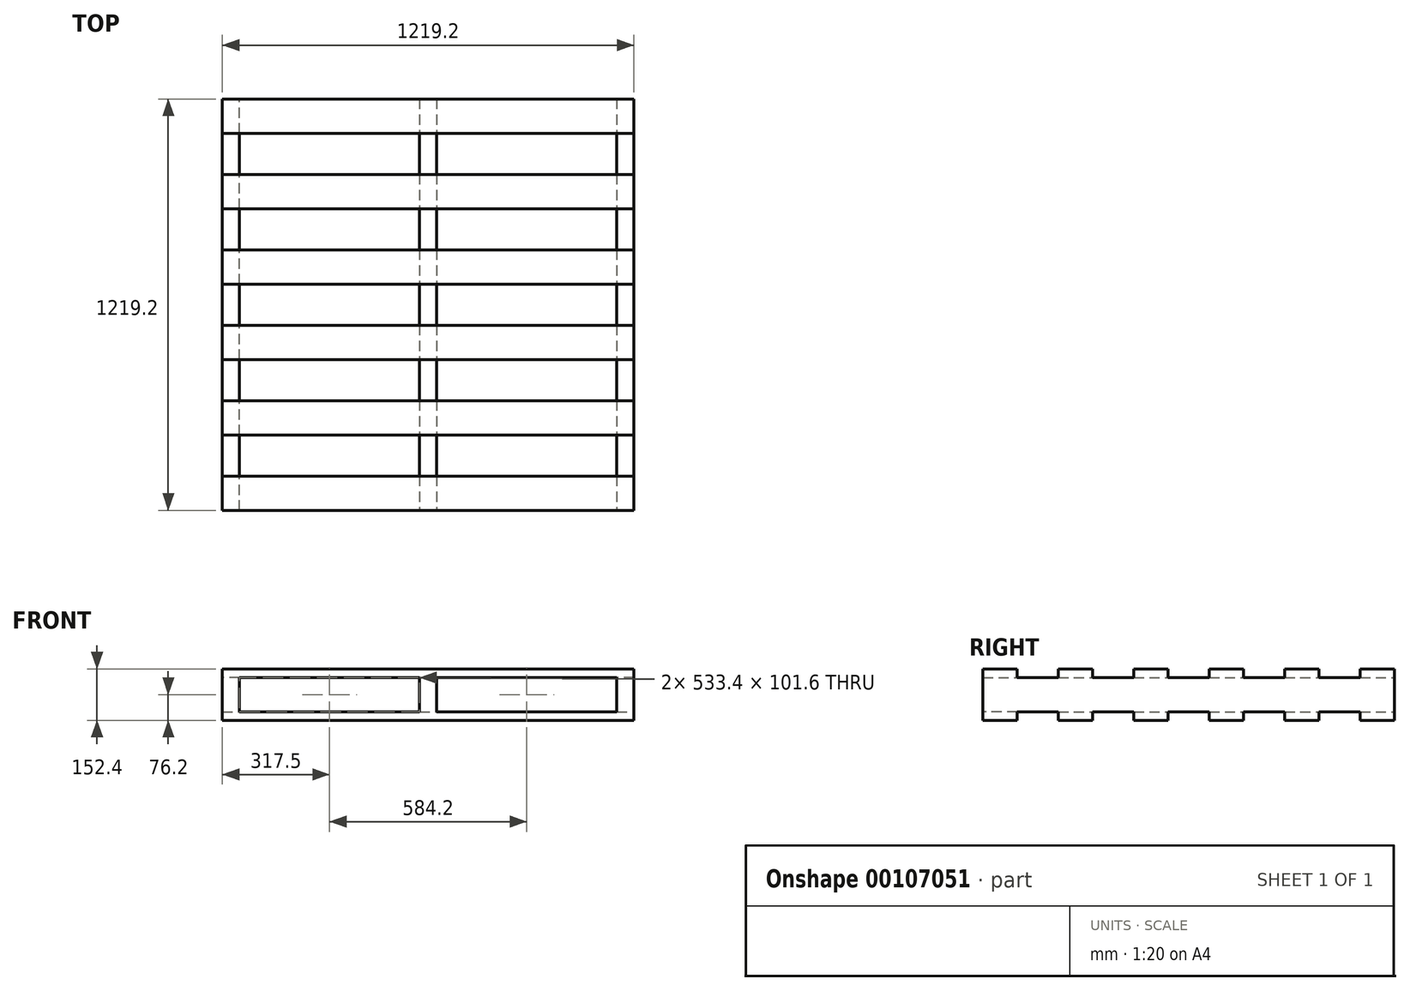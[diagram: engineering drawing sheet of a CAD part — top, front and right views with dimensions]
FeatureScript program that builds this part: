
annotation { "Feature Type Name" : "Feature", "Feature Type Description" : "" }
export const myFeature = defineFeature(function(context is Context, id is Id, definition is map)
    precondition{}
    {
        {
            var Q0;
            Q0=qCreatedBy(makeId("Top.planeOp"),FACE);
            var sketch = newSketch(context, id + "F0", { "sketchPlane" : qUnion([Q0])});
            skLineSegment(sketch, "E0.bottom", {"start": v(0, 0) * mm, "end": v(1219.2, 0) * mm, "construction": true});
            skLineSegment(sketch, "E0.top", {"start": v(0, 1219.2) * mm, "end": v(1219.2, 1219.2) * mm, "construction": true});
            skLineSegment(sketch, "E0.left", {"start": v(0, 0) * mm, "end": v(0, 1219.2) * mm, "construction": true});
            skLineSegment(sketch, "E0.right", {"start": v(1219.2, 0) * mm, "end": v(1219.2, 1219.2) * mm, "construction": true});
            skLineSegment(sketch, "E1.bottom", {"start": v(0, 0) * mm, "end": v(1219.2, 0) * mm});
            skLineSegment(sketch, "E1.top", {"start": v(0, 101.6) * mm, "end": v(1219.2, 101.6) * mm});
            skLineSegment(sketch, "E1.left", {"start": v(0, 0) * mm, "end": v(0, 101.6) * mm});
            skLineSegment(sketch, "E1.right", {"start": v(1219.2, 0) * mm, "end": v(1219.2, 101.6) * mm});
            skLineSegment(sketch, "E2.bottom", {"start": v(0, 325.12) * mm, "end": v(1219.2, 325.12) * mm});
            skLineSegment(sketch, "E2.top", {"start": v(0, 223.52) * mm, "end": v(1219.2, 223.52) * mm});
            skLineSegment(sketch, "E2.left", {"start": v(0, 325.12) * mm, "end": v(0, 223.52) * mm});
            skLineSegment(sketch, "E2.right", {"start": v(1219.2, 325.12) * mm, "end": v(1219.2, 223.52) * mm});
            skLineSegment(sketch, "E3", {"start": v(609.6, 101.6) * mm, "end": v(609.6, 223.52) * mm});
            skLineSegment(sketch, "E4.bottom", {"start": v(0, 447.04) * mm, "end": v(1219.2, 447.04) * mm});
            skLineSegment(sketch, "E4.top", {"start": v(0, 548.64) * mm, "end": v(1219.2, 548.64) * mm});
            skLineSegment(sketch, "E4.left", {"start": v(0, 447.04) * mm, "end": v(0, 548.64) * mm});
            skLineSegment(sketch, "E4.right", {"start": v(1219.2, 447.04) * mm, "end": v(1219.2, 548.64) * mm});
            skLineSegment(sketch, "E5", {"start": v(609.6, 325.12) * mm, "end": v(609.6, 447.04) * mm});
            skLineSegment(sketch, "E6.bottom", {"start": v(0, 670.56) * mm, "end": v(1219.2, 670.56) * mm});
            skLineSegment(sketch, "E6.top", {"start": v(0, 772.16) * mm, "end": v(1219.2, 772.16) * mm});
            skLineSegment(sketch, "E6.left", {"start": v(0, 670.56) * mm, "end": v(0, 772.16) * mm});
            skLineSegment(sketch, "E6.right", {"start": v(1219.2, 670.56) * mm, "end": v(1219.2, 772.16) * mm});
            skLineSegment(sketch, "E7.bottom", {"start": v(0, 894.08) * mm, "end": v(1219.2, 894.08) * mm});
            skLineSegment(sketch, "E7.top", {"start": v(0, 995.68) * mm, "end": v(1219.2, 995.68) * mm});
            skLineSegment(sketch, "E7.left", {"start": v(0, 894.08) * mm, "end": v(0, 995.68) * mm});
            skLineSegment(sketch, "E7.right", {"start": v(1219.2, 894.08) * mm, "end": v(1219.2, 995.68) * mm});
            skLineSegment(sketch, "E8.bottom", {"start": v(0, 1219.2) * mm, "end": v(1219.2, 1219.2) * mm});
            skLineSegment(sketch, "E8.top", {"start": v(0, 1117.6) * mm, "end": v(1219.2, 1117.6) * mm});
            skLineSegment(sketch, "E8.left", {"start": v(0, 1219.2) * mm, "end": v(0, 1117.6) * mm});
            skLineSegment(sketch, "E8.right", {"start": v(1219.2, 1219.2) * mm, "end": v(1219.2, 1117.6) * mm});
            skLineSegment(sketch, "E9", {"start": v(609.6, 1117.6) * mm, "end": v(609.6, 995.68) * mm});
            skLineSegment(sketch, "E10", {"start": v(609.6, 894.08) * mm, "end": v(609.6, 772.16) * mm});
            skLineSegment(sketch, "E11", {"start": v(609.6, 670.56) * mm, "end": v(609.6, 548.64) * mm});
            skSolve(sketch);
        }
        {
            var Q0;
            Q0=makeQuery(id+"F0.imprint","IMPRINT",FACE,{"disambiguationData":[TD([[makeQuery(id+"F0.imprint","IMPRINT",EDGE,{"derivedFrom":sQuery(id+"F0.wireOp",EDGE,"E1.bottom")}),1.0]])]});
            extrude(context, id + "F1", {"entities" : qUnion([Q0]), "depth" : 25.4 * mm});
        }
        {
            var Q0;
            Q0=makeQuery(id+"F1.opExtrude","CAP_FACE",FACE,{"disambiguationData":[OSD([sQuery(id+"F0.wireOp",EDGE,"E1.bottom"),sQuery(id+"F0.wireOp",EDGE,"E1.top"),sQuery(id+"F0.wireOp",EDGE,"E1.left"),sQuery(id+"F0.wireOp",EDGE,"E1.right")])],"isStart":false});
            var sketch = newSketch(context, id + "F2", { "sketchPlane" : qUnion([Q0])});
            skLineSegment(sketch, "E12.0", {"start": v(0, 1219.2) * mm, "end": v(1219.2, 1219.2) * mm, "construction": true});
            skLineSegment(sketch, "E13.0", {"start": v(0, 0) * mm, "end": v(1219.2, 0) * mm, "construction": true});
            skLineSegment(sketch, "E14.bottom", {"start": v(0, 0) * mm, "end": v(50.8, 0) * mm});
            skLineSegment(sketch, "E14.top", {"start": v(0, 1219.2) * mm, "end": v(50.8, 1219.2) * mm});
            skLineSegment(sketch, "E14.left", {"start": v(0, 0) * mm, "end": v(0, 1219.2) * mm});
            skLineSegment(sketch, "E14.right", {"start": v(50.8, 0) * mm, "end": v(50.8, 1219.2) * mm});
            skLineSegment(sketch, "E15.bottom", {"start": v(609.6, 1219.2) * mm, "end": v(635, 1219.2) * mm});
            skLineSegment(sketch, "E15.top", {"start": v(609.6, 0) * mm, "end": v(635, 0) * mm});
            skLineSegment(sketch, "E15.left", {"start": v(609.6, 1219.2) * mm, "end": v(609.6, 0) * mm});
            skLineSegment(sketch, "E15.right", {"start": v(635, 1219.2) * mm, "end": v(635, 0) * mm});
            skLineSegment(sketch, "E16.bottom", {"start": v(1219.2, 1219.2) * mm, "end": v(1168.4, 1219.2) * mm});
            skLineSegment(sketch, "E16.top", {"start": v(1219.2, 0) * mm, "end": v(1168.4, 0) * mm});
            skLineSegment(sketch, "E16.left", {"start": v(1219.2, 1219.2) * mm, "end": v(1219.2, 0) * mm});
            skLineSegment(sketch, "E16.right", {"start": v(1168.4, 1219.2) * mm, "end": v(1168.4, 0) * mm});
            skLineSegment(sketch, "E17.bottom", {"start": v(609.6, 1219.2) * mm, "end": v(584.2, 1219.2) * mm});
            skLineSegment(sketch, "E17.top", {"start": v(609.6, 0) * mm, "end": v(584.2, 0) * mm});
            skLineSegment(sketch, "E17.left", {"start": v(609.6, 1219.2) * mm, "end": v(609.6, 0) * mm, "construction": true});
            skLineSegment(sketch, "E17.right", {"start": v(584.2, 1219.2) * mm, "end": v(584.2, 0) * mm});
            skSolve(sketch);
        }
        {
            var Q0;
            Q0 = qSketchRegion(id + "F2", true);
            extrude(context, id + "F3", {"entities" : qUnion([Q0]), "operationType" : NewBodyOperationType.ADD, "depth" : 101.6 * mm});
        }
        {
            var Q0;
            Q0=makeQuery(id+"F3.opExtrude","CAP_FACE",FACE,{"disambiguationData":[OSD([sQuery(id+"F2.wireOp",EDGE,"E14.bottom"),sQuery(id+"F2.wireOp",EDGE,"E14.top"),sQuery(id+"F2.wireOp",EDGE,"E14.left"),sQuery(id+"F2.wireOp",EDGE,"E14.right")])],"isStart":false});
            var sketch = newSketch(context, id + "F4", { "sketchPlane" : qUnion([Q0])});
            skLineSegment(sketch, "E18.0.0", {"start": v(1219.2, 1219.2) * mm, "end": v(0, 1219.2) * mm});
            skLineSegment(sketch, "E18.0.1", {"start": v(0, 1219.2) * mm, "end": v(0, 1117.6) * mm});
            skLineSegment(sketch, "E18.0.2", {"start": v(0, 1117.6) * mm, "end": v(1219.2, 1117.6) * mm});
            skLineSegment(sketch, "E18.0.3", {"start": v(1219.2, 1117.6) * mm, "end": v(1219.2, 1219.2) * mm});
            skLineSegment(sketch, "E19.0.0", {"start": v(0, 995.68) * mm, "end": v(0, 894.08) * mm});
            skLineSegment(sketch, "E19.0.1", {"start": v(0, 894.08) * mm, "end": v(1219.2, 894.08) * mm});
            skLineSegment(sketch, "E19.0.2", {"start": v(1219.2, 894.08) * mm, "end": v(1219.2, 995.68) * mm});
            skLineSegment(sketch, "E19.0.3", {"start": v(1219.2, 995.68) * mm, "end": v(0, 995.68) * mm});
            skLineSegment(sketch, "E20.0.0", {"start": v(0, 772.16) * mm, "end": v(0, 670.56) * mm});
            skLineSegment(sketch, "E20.0.1", {"start": v(0, 670.56) * mm, "end": v(1219.2, 670.56) * mm});
            skLineSegment(sketch, "E20.0.2", {"start": v(1219.2, 670.56) * mm, "end": v(1219.2, 772.16) * mm});
            skLineSegment(sketch, "E20.0.3", {"start": v(1219.2, 772.16) * mm, "end": v(0, 772.16) * mm});
            skLineSegment(sketch, "E21.0.0", {"start": v(0, 548.64) * mm, "end": v(0, 447.04) * mm});
            skLineSegment(sketch, "E21.0.1", {"start": v(0, 447.04) * mm, "end": v(1219.2, 447.04) * mm});
            skLineSegment(sketch, "E21.0.2", {"start": v(1219.2, 447.04) * mm, "end": v(1219.2, 548.64) * mm});
            skLineSegment(sketch, "E21.0.3", {"start": v(1219.2, 548.64) * mm, "end": v(0, 548.64) * mm});
            skLineSegment(sketch, "E22.0.0", {"start": v(1219.2, 325.12) * mm, "end": v(0, 325.12) * mm});
            skLineSegment(sketch, "E22.0.1", {"start": v(0, 325.12) * mm, "end": v(0, 223.52) * mm});
            skLineSegment(sketch, "E22.0.2", {"start": v(0, 223.52) * mm, "end": v(1219.2, 223.52) * mm});
            skLineSegment(sketch, "E22.0.3", {"start": v(1219.2, 223.52) * mm, "end": v(1219.2, 325.12) * mm});
            skLineSegment(sketch, "E23.0.0", {"start": v(0, 101.6) * mm, "end": v(0, 0) * mm});
            skLineSegment(sketch, "E23.0.1", {"start": v(0, 0) * mm, "end": v(1219.2, 0) * mm});
            skLineSegment(sketch, "E23.0.2", {"start": v(1219.2, 0) * mm, "end": v(1219.2, 101.6) * mm});
            skLineSegment(sketch, "E23.0.3", {"start": v(1219.2, 101.6) * mm, "end": v(0, 101.6) * mm});
            skSolve(sketch);
        }
        {
            var Q0;
            Q0 = qSketchRegion(id + "F4", true);
            extrude(context, id + "F5", {"entities" : qUnion([Q0]), "operationType" : NewBodyOperationType.ADD, "depth" : 25.4 * mm});
        }
        {
            var Q0;
            Q0=makeQuery(id+"F3.opExtrude","CAP_FACE",FACE,{"disambiguationData":[OSD([sQuery(id+"F2.wireOp",EDGE,"E16.bottom"),sQuery(id+"F2.wireOp",EDGE,"E16.top"),sQuery(id+"F2.wireOp",EDGE,"E16.left"),sQuery(id+"F2.wireOp",EDGE,"E16.right")])],"isStart":true});
            var sketch = newSketch(context, id + "F6", { "sketchPlane" : qUnion([Q0])});
            skLineSegment(sketch, "E24.0.0", {"start": v(609.6, -325.12) * mm, "end": v(0, -325.12) * mm});
            skLineSegment(sketch, "E24.0.1", {"start": v(0, -325.12) * mm, "end": v(0, -223.52) * mm});
            skLineSegment(sketch, "E24.0.2", {"start": v(0, -223.52) * mm, "end": v(609.6, -223.52) * mm});
            skLineSegment(sketch, "E24.0.3", {"start": v(609.6, -223.52) * mm, "end": v(1219.2, -223.52) * mm});
            skLineSegment(sketch, "E24.0.4", {"start": v(1219.2, -223.52) * mm, "end": v(1219.2, -325.12) * mm});
            skLineSegment(sketch, "E24.0.5", {"start": v(1219.2, -325.12) * mm, "end": v(609.6, -325.12) * mm});
            skLineSegment(sketch, "E25.0.0", {"start": v(0, -548.64) * mm, "end": v(0, -447.04) * mm});
            skLineSegment(sketch, "E25.0.1", {"start": v(0, -447.04) * mm, "end": v(609.6, -447.04) * mm});
            skLineSegment(sketch, "E25.0.2", {"start": v(609.6, -447.04) * mm, "end": v(1219.2, -447.04) * mm});
            skLineSegment(sketch, "E25.0.3", {"start": v(1219.2, -447.04) * mm, "end": v(1219.2, -548.64) * mm});
            skLineSegment(sketch, "E25.0.4", {"start": v(1219.2, -548.64) * mm, "end": v(609.6, -548.64) * mm});
            skLineSegment(sketch, "E25.0.5", {"start": v(609.6, -548.64) * mm, "end": v(0, -548.64) * mm});
            skLineSegment(sketch, "E26.0.0", {"start": v(0, -772.16) * mm, "end": v(0, -670.56) * mm});
            skLineSegment(sketch, "E26.0.1", {"start": v(0, -670.56) * mm, "end": v(609.6, -670.56) * mm});
            skLineSegment(sketch, "E26.0.2", {"start": v(609.6, -670.56) * mm, "end": v(1219.2, -670.56) * mm});
            skLineSegment(sketch, "E26.0.3", {"start": v(1219.2, -670.56) * mm, "end": v(1219.2, -772.16) * mm});
            skLineSegment(sketch, "E26.0.4", {"start": v(1219.2, -772.16) * mm, "end": v(609.6, -772.16) * mm});
            skLineSegment(sketch, "E26.0.5", {"start": v(609.6, -772.16) * mm, "end": v(0, -772.16) * mm});
            skLineSegment(sketch, "E27.0.0", {"start": v(0, -995.68) * mm, "end": v(0, -894.08) * mm});
            skLineSegment(sketch, "E27.0.1", {"start": v(0, -894.08) * mm, "end": v(609.6, -894.08) * mm});
            skLineSegment(sketch, "E27.0.2", {"start": v(609.6, -894.08) * mm, "end": v(1219.2, -894.08) * mm});
            skLineSegment(sketch, "E27.0.3", {"start": v(1219.2, -894.08) * mm, "end": v(1219.2, -995.68) * mm});
            skLineSegment(sketch, "E27.0.4", {"start": v(1219.2, -995.68) * mm, "end": v(609.6, -995.68) * mm});
            skLineSegment(sketch, "E27.0.5", {"start": v(609.6, -995.68) * mm, "end": v(0, -995.68) * mm});
            skLineSegment(sketch, "E28.0.0", {"start": v(1219.2, -1219.2) * mm, "end": v(0, -1219.2) * mm});
            skLineSegment(sketch, "E28.0.1", {"start": v(0, -1219.2) * mm, "end": v(0, -1117.6) * mm});
            skLineSegment(sketch, "E28.0.2", {"start": v(0, -1117.6) * mm, "end": v(609.6, -1117.6) * mm});
            skLineSegment(sketch, "E28.0.3", {"start": v(609.6, -1117.6) * mm, "end": v(1219.2, -1117.6) * mm});
            skLineSegment(sketch, "E28.0.4", {"start": v(1219.2, -1117.6) * mm, "end": v(1219.2, -1219.2) * mm});
            skSolve(sketch);
        }
        {
            var Q0;
            Q0 = qSketchRegion(id + "F6", true);
            extrude(context, id + "F7", {"entities" : qUnion([Q0]), "operationType" : NewBodyOperationType.ADD, "depth" : 25.4 * mm});
        }
    });
